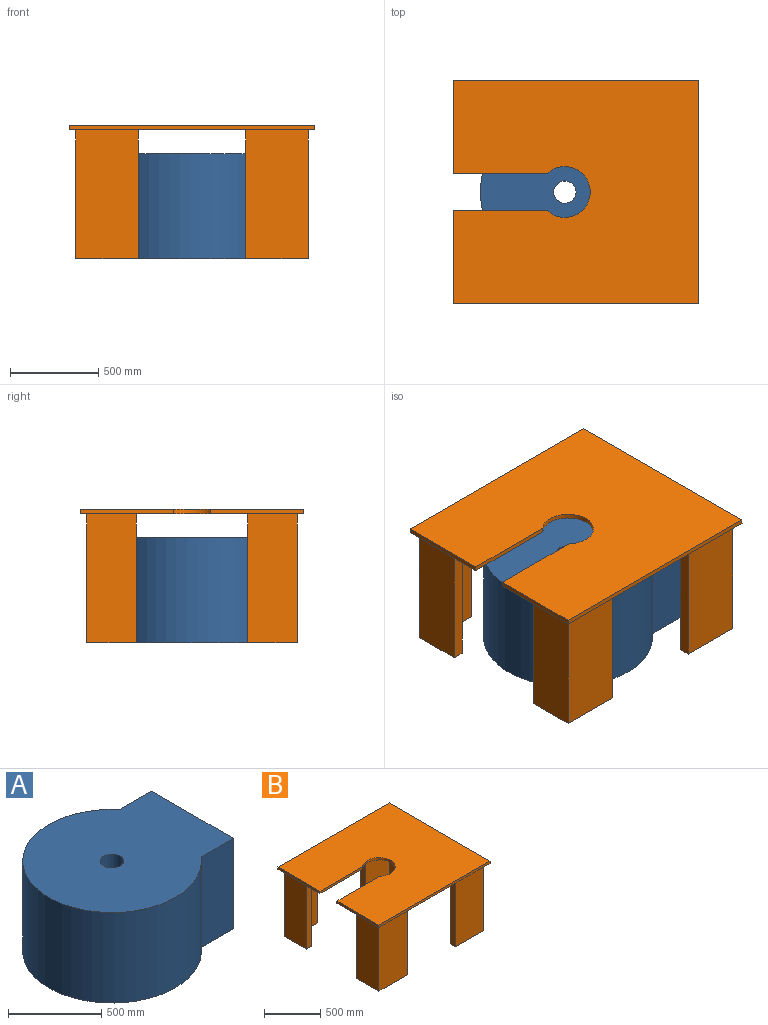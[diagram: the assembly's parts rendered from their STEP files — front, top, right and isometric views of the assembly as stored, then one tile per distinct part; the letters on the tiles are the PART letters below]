
ASSEMBLY  parts=2 mates=1
PART A: 7 faces, bbox 1089.3x959.5x594.6 mm
  f0: plane 622.3x594.61mm, normal (1,0,0), area 370028.3mm2, adj f1,f3,f5,f6
  f1: plane 594.61x244.44mm, normal (0,1,0), area 145350.1mm2, adj f0,f2,f5,f6
  f2: cylinder r=479.74mm len=959.49mm, axis (0,0,-1), area 1389725.6mm2, adj f1,f3,f5,f6
  f3: plane 594.61x244.44mm, normal (0,-1,0), area 145350.1mm2, adj f0,f2,f5,f6
  f4: cylinder r=63.5mm len=594.61mm, axis (0,0,-1), area 237240.4mm2, adj f5,f6
  f5: plane 1089.34x959.49mm, normal (0,0,1), area 813692.8mm2, adj f0,f1,f2,f3,f4
  f6: plane 1089.34x959.49mm, normal (0,0,-1), area 813692.8mm2, adj f0,f1,f2,f3,f4
PART B: 38 faces, bbox 1397x1270x755.7 mm
  f0: plane 730.25x355.6mm, normal (0,-1,0), area 259676.9mm2, adj f1,f5,f6,f29
  f1: plane 730.25x279.4mm, normal (1,0,0), area 204031.9mm2, adj f0,f2,f6,f29
  f2: plane 730.25x63.5mm, normal (0,1,0), area 46370.9mm2, adj f1,f3,f6,f29
  f3: plane 730.25x215.9mm, normal (-1,0,0), area 157661mm2, adj f2,f4,f6,f29
  f4: plane 730.25x292.1mm, normal (0,1,0), area 213306mm2, adj f3,f5,f6,f29
  f5: plane 730.25x63.5mm, normal (-1,0,0), area 46370.9mm2, adj f0,f4,f6,f29
  f6: plane 355.6x279.4mm, normal (0,0,-1), area 36290.2mm2, adj f0,f1,f2,f3,f4,f5
  f7: plane 730.25x355.6mm, normal (0,-1,0), area 259676.9mm2, adj f8,f12,f13,f29
  f8: plane 730.25x63.5mm, normal (1,0,0), area 46370.9mm2, adj f7,f9,f13,f29
  f9: plane 730.25x292.1mm, normal (0,1,0), area 213306mm2, adj f8,f10,f13,f29
  f10: plane 730.25x215.9mm, normal (1,0,0), area 157661mm2, adj f9,f11,f13,f29
  f11: plane 730.25x63.5mm, normal (0,1,0), area 46370.9mm2, adj f10,f12,f13,f29
  f12: plane 730.25x279.4mm, normal (-1,0,0), area 204031.9mm2, adj f7,f11,f13,f29
  f13: plane 355.6x279.4mm, normal (0,0,-1), area 36290.2mm2, adj f7,f8,f9,f10,f11,f12
  f14: plane 730.25x355.6mm, normal (0,1,0), area 259676.9mm2, adj f15,f19,f20,f29
  f15: plane 730.25x63.5mm, normal (-1,0,0), area 46370.9mm2, adj f14,f16,f20,f29
  f16: plane 730.25x292.1mm, normal (0,-1,0), area 213306mm2, adj f15,f17,f20,f29
  f17: plane 730.25x215.9mm, normal (-1,0,0), area 157661mm2, adj f16,f18,f20,f29
  f18: plane 730.25x63.5mm, normal (0,-1,0), area 46370.9mm2, adj f17,f19,f20,f29
  f19: plane 730.25x279.4mm, normal (1,0,0), area 204031.9mm2, adj f14,f18,f20,f29
  f20: plane 355.6x279.4mm, normal (0,0,-1), area 36290.2mm2, adj f14,f15,f16,f17,f18,f19
  f21: plane 537.87x25.4mm, normal (0,1,0), area 13662mm2, adj f22,f28,f29,f37
  f22: plane 528.32x25.4mm, normal (-1,0,0), area 13419.3mm2, adj f21,f23,f29,f37
  f23: plane 1397x25.4mm, normal (0,-1,0), area 35483.8mm2, adj f22,f24,f29,f37
  f24: plane 1270x25.4mm, normal (1,0,0), area 32258mm2, adj f23,f25,f29,f37
  f25: plane 1397x25.4mm, normal (0,1,0), area 35483.8mm2, adj f24,f26,f29,f37
  f26: plane 528.32x25.4mm, normal (-1,0,0), area 13419.3mm2, adj f25,f27,f29,f37
  f27: plane 537.87x25.4mm, normal (0,-1,0), area 13662mm2, adj f26,f28,f29,f37
  f28: cylinder r=144.27mm len=288.54mm, axis (0,0,1), area 16925.3mm2, adj f21,f27,f29,f37
  f29: plane 1397x1270mm, normal (0,0,-1), area 1455839mm2, adj f0,f1,f2,f3,f4,f5,f7,f8
  f30: plane 355.6x279.4mm, normal (0,0,-1), area 36290.2mm2, adj f31,f32,f33,f34,f35,f36
  f31: plane 730.25x63.5mm, normal (1,0,0), area 46370.9mm2, adj f29,f30,f32,f36
  f32: plane 730.25x292.1mm, normal (0,-1,0), area 213306mm2, adj f29,f30,f31,f33
  f33: plane 730.25x215.9mm, normal (1,0,0), area 157661mm2, adj f29,f30,f32,f34
  f34: plane 730.25x63.5mm, normal (0,-1,0), area 46370.9mm2, adj f29,f30,f33,f35
  f35: plane 730.25x279.4mm, normal (-1,0,0), area 204031.9mm2, adj f29,f30,f34,f36
  f36: plane 730.25x355.6mm, normal (0,1,0), area 259676.9mm2, adj f29,f30,f31,f35
  f37: plane 1397x1270mm, normal (0,0,1), area 1601000mm2, adj f21,f22,f23,f24,f25,f26,f27,f28
PLACE A t=(455.01,-281.68,-183.66)mm
PLACE B rot(axis=(-0.02,-0.99,0.12),0deg) t=(455.01,-281.68,571.99)mm
MATE slider A.f4 <-> B.f28  axis (0,0,-1) through (455.01,-281.68,113.65)mm
